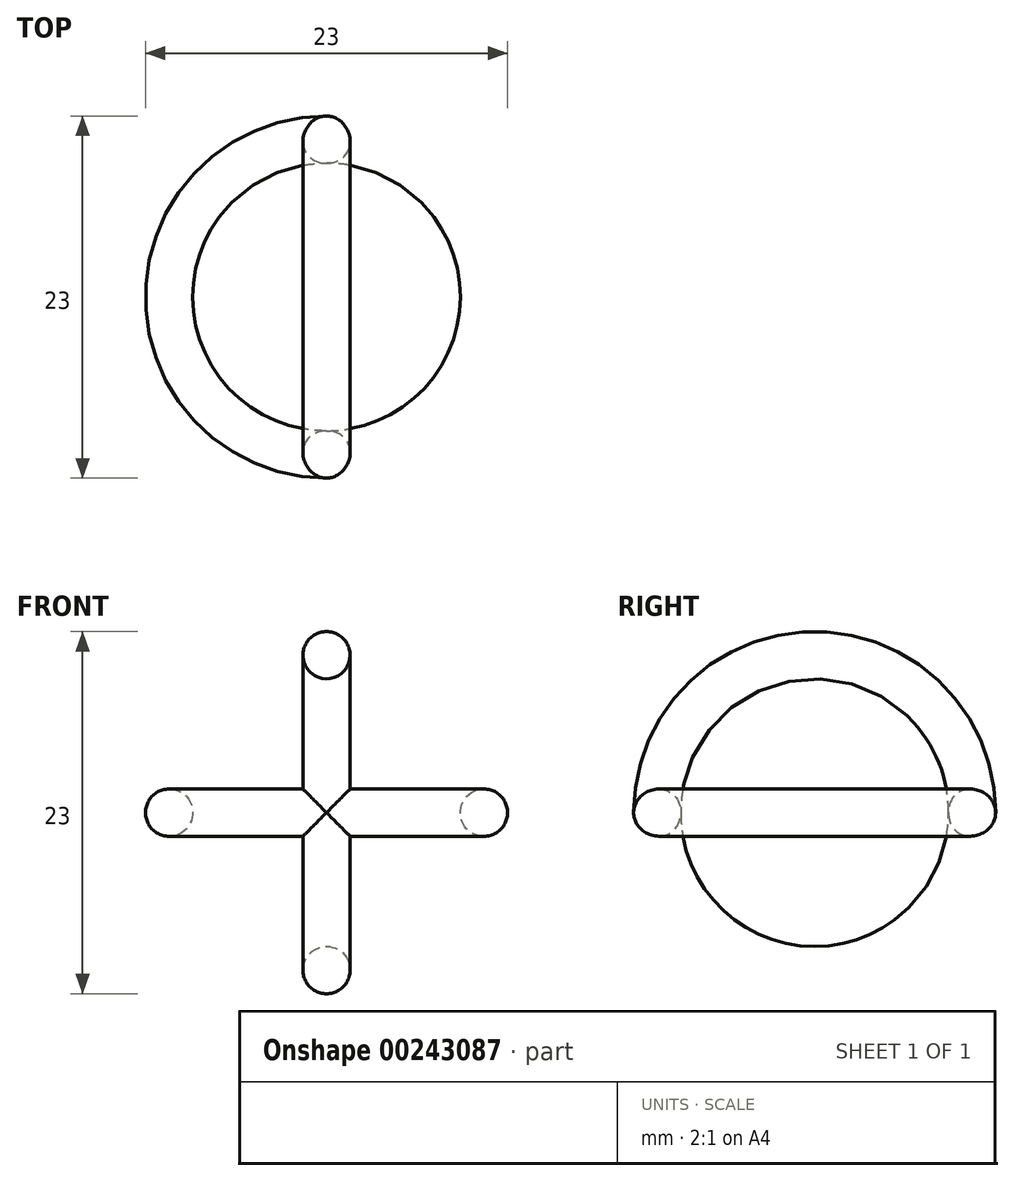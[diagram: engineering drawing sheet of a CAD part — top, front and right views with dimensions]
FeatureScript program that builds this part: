
annotation { "Feature Type Name" : "Feature", "Feature Type Description" : "" }
export const myFeature = defineFeature(function(context is Context, id is Id, definition is map)
    precondition{}
    {
        {
            var Q0;
            Q0=qCreatedBy(makeId("Front.planeOp"),FACE);
            var sketch = newSketch(context, id + "F0", { "sketchPlane" : qUnion([Q0])});
            skLineSegment(sketch, "E0", {"start": v(0, 0) * mm, "end": v(10, 0) * mm, "construction": true});
            skLineSegment(sketch, "E1", {"start": v(0, 0) * mm, "end": v(0, 10) * mm, "construction": true});
            skCircle(sketch, "E2", {"center": v(0, 10) * mm, "radius": 1.5 * mm});
            skCircle(sketch, "E3", {"center": v(10, 0) * mm, "radius": 1.5 * mm});
            skSolve(sketch);
        }
        {
            var Q0;
            Q0=makeQuery(id+"F0.imprint","IMPRINT",FACE,{"disambiguationData":[TD([[makeQuery(id+"F0.imprint","IMPRINT",EDGE,{"derivedFrom":sQuery(id+"F0.wireOp",EDGE,"E2")}),1.0]])]});
            var Q1;
            Q1=sQuery(id+"F0.wireOp",EDGE,"E0");
            revolve(context, id + "F1", {"entities" : qUnion([Q0]), "axis" : qUnion([Q1]), "revolveType" : RevolveType.FULL});
        }
        {
            var Q0;
            Q0=makeQuery(id+"F0.imprint","IMPRINT",FACE,{"disambiguationData":[TD([[makeQuery(id+"F0.imprint","IMPRINT",EDGE,{"derivedFrom":sQuery(id+"F0.wireOp",EDGE,"E3")}),1.0]])]});
            var Q1;
            Q1=sQuery(id+"F0.wireOp",EDGE,"E3");
            var Q2;
            Q2=sQuery(id+"F0.wireOp",EDGE,"E1");
            revolve(context, id + "F2", {"operationType" : NewBodyOperationType.ADD, "entities" : qUnion([Q0]), "surfaceEntities" : qUnion([Q1]), "axis" : qUnion([Q2]), "revolveType" : RevolveType.FULL});
        }
    });
